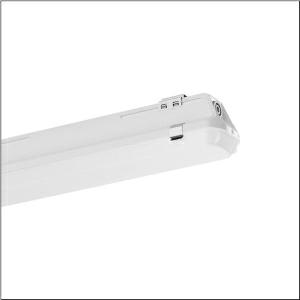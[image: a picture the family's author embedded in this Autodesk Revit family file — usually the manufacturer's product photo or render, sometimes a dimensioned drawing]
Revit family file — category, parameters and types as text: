
# Revit family: monsun_r__11_51fp10mp480h_5fdf
name_source: partatom
category: Lighting Fixtures
units: mm (PartAtom-declared; Revit-internal decimal feet)

## family parameters
Cut with Voids When Loaded = No
Host = Face
Light Source = No
Part Type = Normal
Room Calculation Point = No
Round Connector Dimension = Use Diameter
Shared = No

## types (1)
- --- (1 x LED, 8070 lm, 45.4 W, 4000K)
    Apparent Load = 45 VA
    CIE Flux Codes = 47 77 93 94 100
    Color Rendering = 80
    Color Temperature = 4000K
    Default Elevation = 1800 mm
    Description = Monsun® 11, damp-proof luminaire, chain hanger, primary optical cover: enclosure, of PMMA, light emission: direct distribution, primary light characteristic: symmetric, installation type: suspended mounting, surface-mounted, horizontal mounting, vertical mounting, LED, rated luminous flux: 8.070lm, luminous efficacy: 178lm/W, light colour: 840, colour temperature: 4000K, control gear: ECG, with terminal, 3-pole, max. 2.5mm², mains connection: 220..240V, AC, 50/60Hz, rated input power: 45W, luminaire housing, of glass-fibre reinforced polyester, uncoated, bright grey, incl. chain hanger, length: 1.590mm, width: 90mm, height: 88mm, clip for enclosure, of stainless steel (V2A), ceiling mounting element, of stainless steel (V2A), chain hanger, of stainless steel (V2A), protection rating (complete): IP66, insulation class (complete): insulation class I (protective earthing), certification: CE, ENEC, VDE, UKCA, protection symbol: D, impact resistance: IK04, permissible operating ambient temperature: -35..+40°C, standard: EN 50419, EN 60598-2-1, no direct snow, no direct sun, no direct rain, for indoor or canopied outdoor use, corresponds to IFS (International Featured Standards) requirements for safety and quality in the food industry, contact your sales advisor before using the luminaires in applications with unclear chemical exposure, large temperature fluctuations or condensation-forming humidity, LABS conformity tested according to VDMA 24364:2018-05, packaging unit: 1 piece
    Height = 89 mm
    Lamp = 1 x LED
    Lamp Light Flux = 8070 lm
    Lamp Power = 45.4 W
    Lamp count = 1
    Length = 1590 mm
    Luminous efficacy = 178 lm/W
    Manufacturer = Siteco
    ModVariant = No
    Model = 51FP10MP480H
    Mounting Place = Ceiling
    Mounting Type = Surface mounted
    Number of Poles = 1
    OnlyDefault = Yes
    Power Factor = 1
    Product Name = Monsun® 11
    Product group = damp-proof luminaire
    ProductGroupID = 301
    Protection Class = Protection class I
    Protection Degree = IP 66
    RLX_Detail_Level = 1
    RLX_Emergency_Light_Flux = 0 lm
    RLX_Emergency_Type = 0
    RLX_Emergency_Type_DB = No
    RlxData = <blob elided: 89953 chars, md5=2a6b47ce>
    Socket = socket
    Standby Power = 0 W
    System Light Flux = 8070 lm
    System Power = 45 W
    Type Comments = factory setting: luminous flux: 100 % | (A | C | E) | 105 mA
    Type Image = l_1004748.jpg
    URL = http://relux.com
    VarID = @adj_157447
    Voltage = 0 V
    Weight = 0.00 kg
    Width = 90 mm

## geometry (parser evidence)
native form markers: Blend x4, Sweep x12
no freeform markers — native parametric forms only
